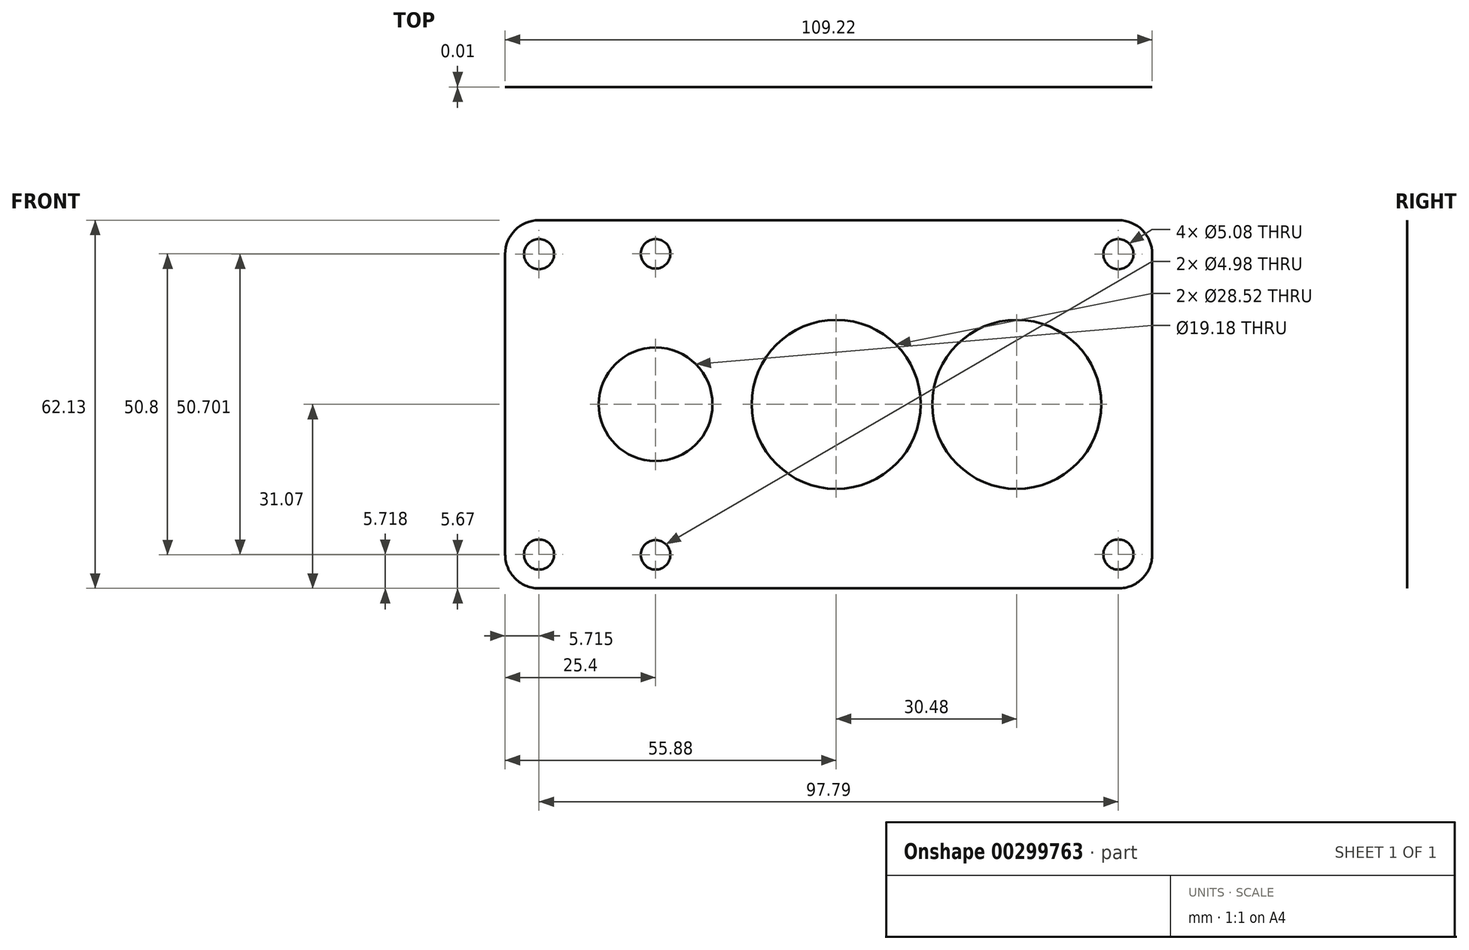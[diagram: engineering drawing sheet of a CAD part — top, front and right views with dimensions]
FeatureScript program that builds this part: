
annotation { "Feature Type Name" : "Feature", "Feature Type Description" : "" }
export const myFeature = defineFeature(function(context is Context, id is Id, definition is map)
    precondition{}
    {
        {
            var Q0;
            Q0=qCreatedBy(makeId("Front.planeOp"),FACE);
            var sketch = newSketch(context, id + "F0", { "sketchPlane" : qUnion([Q0])});
            skCircle(sketch, "E0", {"center": v(0, 0) * mm, "radius": 7.62 * mm, "construction": true});
            skCircle(sketch, "E1", {"center": v(30.48, 0) * mm, "radius": 22.86 * mm, "construction": true});
            skCircle(sketch, "E2", {"center": v(30.48, 0) * mm, "radius": 7.62 * mm, "construction": true});
            skCircle(sketch, "E3", {"center": v(60.96, 0) * mm, "radius": 22.86 * mm, "construction": true});
            skCircle(sketch, "E4", {"center": v(60.96, 0) * mm, "radius": 14.26 * mm});
            skCircle(sketch, "E5", {"center": v(30.48, 0) * mm, "radius": 14.26 * mm});
            skCircle(sketch, "E6", {"center": v(0, 0) * mm, "radius": 9.59 * mm});
            skCircle(sketch, "E7", {"center": v(0, 0) * mm, "radius": 25.4 * mm, "construction": true});
            skCircle(sketch, "E8", {"center": v(0, 25.4) * mm, "radius": 2.49 * mm});
            skCircle(sketch, "E9", {"center": v(0, -25.4) * mm, "radius": 2.49 * mm});
            skCircle(sketch, "E10.0", {"center": v(0, 25.4) * mm, "radius": 5.66 * mm, "construction": true});
            skCircle(sketch, "E11", {"center": v(0, -25.4) * mm, "radius": 5.66 * mm, "construction": true});
            skCircle(sketch, "E12", {"center": v(-19.69, 25.35) * mm, "radius": 2.54 * mm});
            skCircle(sketch, "E13", {"center": v(78.1, 25.35) * mm, "radius": 2.54 * mm});
            skCircle(sketch, "E14", {"center": v(-19.69, -25.35) * mm, "radius": 2.54 * mm});
            skCircle(sketch, "E15", {"center": v(78.1, -25.35) * mm, "radius": 2.54 * mm});
            skLineSegment(sketch, "E16", {"start": v(-19.69, 25.35) * mm, "end": v(-19.68, -25.35) * mm, "construction": true});
            skLineSegment(sketch, "E17", {"start": v(-19.69, -25.35) * mm, "end": v(78.1, -25.35) * mm, "construction": true});
            skLineSegment(sketch, "E18", {"start": v(78.1, -25.35) * mm, "end": v(78.1, 25.35) * mm, "construction": true});
            skLineSegment(sketch, "E19", {"start": v(78.1, 25.35) * mm, "end": v(-19.69, 25.35) * mm, "construction": true});
            skArc(sketch, "E20.0", {"start": v(83.82, 25.35) * mm, "mid": v(82.15, 29.4) * mm, "end": v(78.1, 31.06) * mm});
            skArc(sketch, "E21", {"start": v(78.1, -31.07) * mm, "mid": v(82.15, -29.4) * mm, "end": v(83.82, -25.35) * mm});
            skArc(sketch, "E22", {"start": v(-25.4, -25.35) * mm, "mid": v(-23.66, -29.46) * mm, "end": v(-19.5, -31.06) * mm});
            skArc(sketch, "E23", {"start": v(-19.69, 31.06) * mm, "mid": v(-23.73, 29.4) * mm, "end": v(-25.4, 25.35) * mm});
            skLineSegment(sketch, "E24", {"start": v(83.82, 25.35) * mm, "end": v(83.82, -25.35) * mm});
            skLineSegment(sketch, "E25", {"start": v(-19.69, 31.06) * mm, "end": v(78.1, 31.06) * mm});
            skLineSegment(sketch, "E26", {"start": v(-25.4, 25.35) * mm, "end": v(-25.4, -25.35) * mm});
            skLineSegment(sketch, "E27", {"start": v(-19.87, -31.06) * mm, "end": v(78.1, -31.07) * mm});
            skSolve(sketch);
        }
        {
            var Q0;
            Q0 = qSketchRegion(id + "F0", true);
            extrude(context, id + "F1", {"entities" : qUnion([Q0]), "depth" : 3 / 406.4 * mm});
        }
    });
